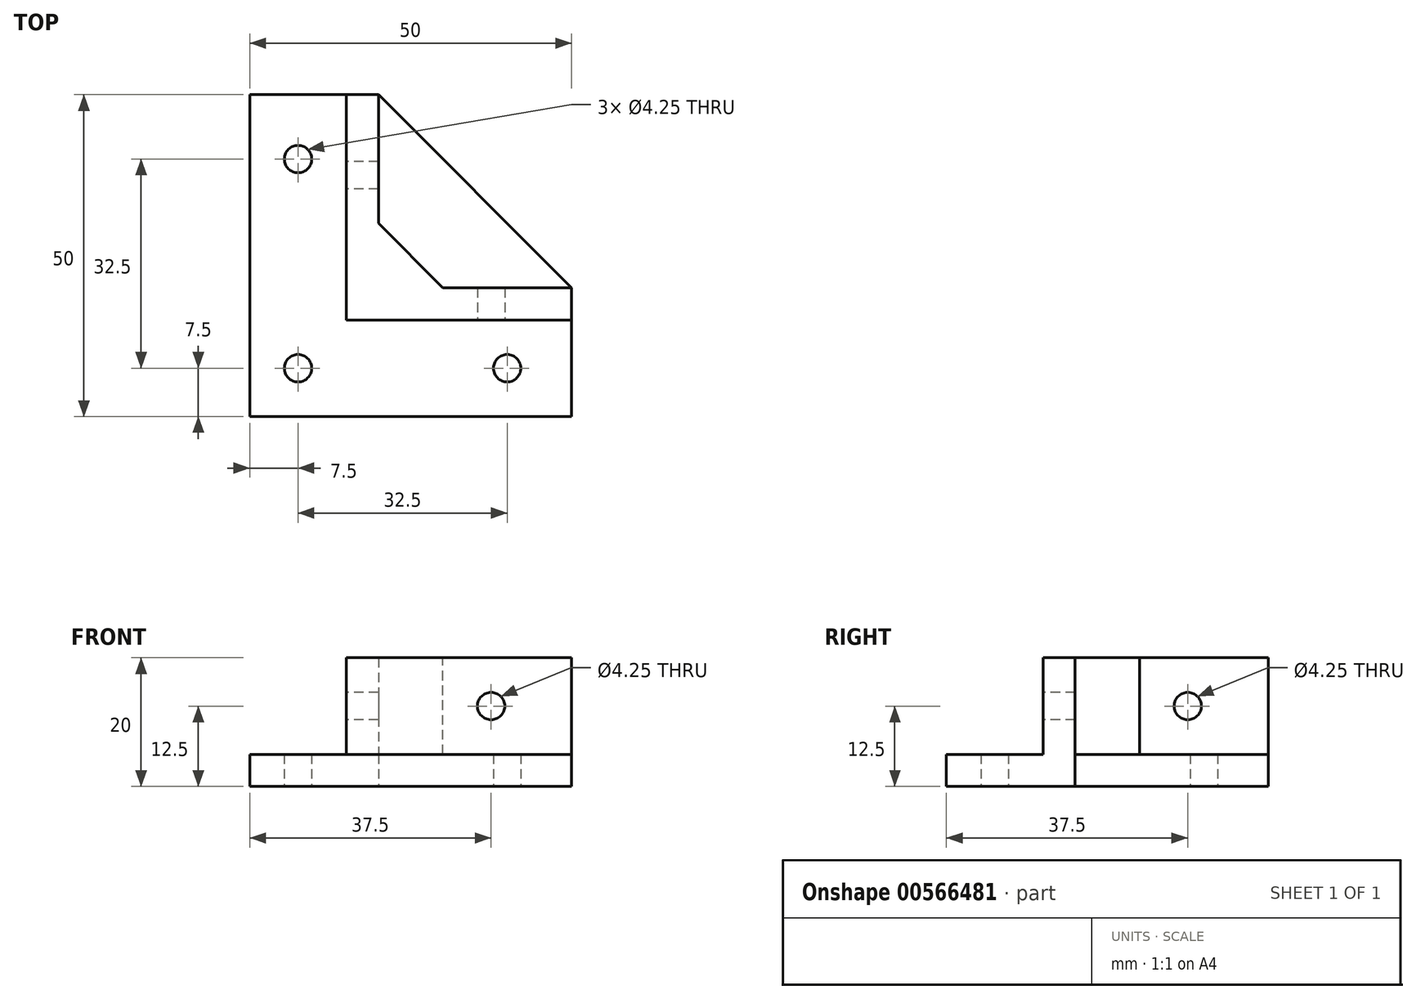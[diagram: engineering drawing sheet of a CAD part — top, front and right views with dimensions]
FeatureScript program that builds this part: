
annotation { "Feature Type Name" : "Feature", "Feature Type Description" : "" }
export const myFeature = defineFeature(function(context is Context, id is Id, definition is map)
    precondition{}
    {
        {
            var Q0;
            Q0=qCreatedBy(makeId("Top.planeOp"),FACE);
            var sketch = newSketch(context, id + "F0", { "sketchPlane" : qUnion([Q0])});
            skLineSegment(sketch, "E0", {"start": v(0, 50) * mm, "end": v(-20, 50) * mm});
            skLineSegment(sketch, "E1", {"start": v(-20, 50) * mm, "end": v(-20, 0) * mm});
            skLineSegment(sketch, "E2", {"start": v(-20, 0) * mm, "end": v(30, 0) * mm});
            skLineSegment(sketch, "E3", {"start": v(30, 0) * mm, "end": v(30, 20) * mm});
            skLineSegment(sketch, "E4", {"start": v(30, 20) * mm, "end": v(0, 20) * mm});
            skLineSegment(sketch, "E5", {"start": v(0, 20) * mm, "end": v(0, 50) * mm});
            skCircle(sketch, "E6", {"center": v(-12.5, 40) * mm, "radius": 2.12 * mm});
            skCircle(sketch, "E7", {"center": v(20, 7.5) * mm, "radius": 2.12 * mm});
            skCircle(sketch, "E8", {"center": v(-12.5, 7.5) * mm, "radius": 2.12 * mm});
            skSolve(sketch);
        }
        {
            var Q0;
            Q0=qSketchRegion(id+"F0",true);
            extrude(context, id + "F1", {"entities" : qUnion([Q0]), "depth" : 5 * mm});
        }
        {
            var Q0;
            Q0=makeQuery(id+"F1.opExtrude","CAP_FACE",FACE,{"disambiguationData":[OSD([sQuery(id+"F0.wireOp",EDGE,"E0"),sQuery(id+"F0.wireOp",EDGE,"E1"),sQuery(id+"F0.wireOp",EDGE,"E2"),sQuery(id+"F0.wireOp",EDGE,"E3"),sQuery(id+"F0.wireOp",EDGE,"E4"),sQuery(id+"F0.wireOp",EDGE,"E5"),sQuery(id+"F0.wireOp",EDGE,"E6"),sQuery(id+"F0.wireOp",EDGE,"E7")])],"isStart":false});
            var sketch = newSketch(context, id + "F2", { "sketchPlane" : qUnion([Q0])});
            skLineSegment(sketch, "E9", {"start": v(0, 50) * mm, "end": v(0, 20) * mm});
            skLineSegment(sketch, "E10", {"start": v(0, 20) * mm, "end": v(30, 20) * mm});
            skLineSegment(sketch, "E11", {"start": v(30, 20) * mm, "end": v(30, 15) * mm});
            skLineSegment(sketch, "E12", {"start": v(30, 15) * mm, "end": v(-5, 15) * mm});
            skLineSegment(sketch, "E13", {"start": v(-5, 15) * mm, "end": v(-5, 50) * mm});
            skLineSegment(sketch, "E14", {"start": v(-5, 50) * mm, "end": v(0, 50) * mm});
            skSolve(sketch);
        }
        {
            var Q0;
            Q0=qSketchRegion(id+"F2",true);
            extrude(context, id + "F3", {"entities" : qUnion([Q0]), "operationType" : NewBodyOperationType.ADD, "depth" : 15 * mm});
        }
        {
            var Q0;
            Q0=makeQuery(id+"F3.opExtrude","SWEPT_FACE",FACE,{"disambiguationData":[OSD([sQuery(id+"F2.wireOp",EDGE,"E13")])]});
            var sketch = newSketch(context, id + "F4", { "sketchPlane" : qUnion([Q0])});
            skCircle(sketch, "E15", {"center": v(-37.5, 12.5) * mm, "radius": 2.12 * mm});
            skSolve(sketch);
        }
        {
            var Q0;
            Q0=qSketchRegion(id+"F4",true);
            extrude(context, id + "F5", {"entities" : qUnion([Q0]), "operationType" : NewBodyOperationType.REMOVE, "oppositeDirection" : true, "depth" : 5 * mm});
        }
        {
            var Q0;
            Q0=makeQuery(id+"F3.opExtrude","SWEPT_FACE",FACE,{"disambiguationData":[OSD([sQuery(id+"F2.wireOp",EDGE,"E12")])]});
            var sketch = newSketch(context, id + "F6", { "sketchPlane" : qUnion([Q0])});
            skCircle(sketch, "E16", {"center": v(17.5, 12.5) * mm, "radius": 2.12 * mm});
            skSolve(sketch);
        }
        {
            var Q0;
            Q0=qSketchRegion(id+"F6",true);
            extrude(context, id + "F7", {"entities" : qUnion([Q0]), "operationType" : NewBodyOperationType.REMOVE, "oppositeDirection" : true, "depth" : 5 * mm});
        }
        {
            var Q0;
            Q0=qCreatedBy(makeId("Top.planeOp"),FACE);
            var sketch = newSketch(context, id + "F8", { "sketchPlane" : qUnion([Q0])});
            skLineSegment(sketch, "E17", {"start": v(0, 50) * mm, "end": v(30, 20) * mm});
            skLineSegment(sketch, "E18", {"start": v(30, 20) * mm, "end": v(0, 20) * mm});
            skLineSegment(sketch, "E19", {"start": v(0, 20) * mm, "end": v(0, 50) * mm});
            skSolve(sketch);
        }
        {
            var Q0;
            Q0=qSketchRegion(id+"F8",true);
            extrude(context, id + "F9", {"entities" : qUnion([Q0]), "operationType" : NewBodyOperationType.ADD, "depth" : 5 * mm});
        }
        {
            var Q0;
            Q0=makeQuery(id+"F3.boolean.opBoolean","MERGE",EDGE,{"derivedFrom":[makeQuery(id+"F1.opExtrude","SWEPT_EDGE",EDGE,{"disambiguationData":[OSD([sQuery(id+"F0.wireOp",EDGE,"E4"),sQuery(id+"F0.wireOp",EDGE,"E5")])]}),makeQuery(id+"F3.opExtrude","SWEPT_EDGE",EDGE,{"disambiguationData":[OSD([sQuery(id+"F2.wireOp",EDGE,"E9"),sQuery(id+"F2.wireOp",EDGE,"E10")])]})]});
            chamfer(context, id + "F10", {"entities" : qUnion([Q0]), "width" : 10 * mm, "tangentPropagation" : true});
        }
    });
